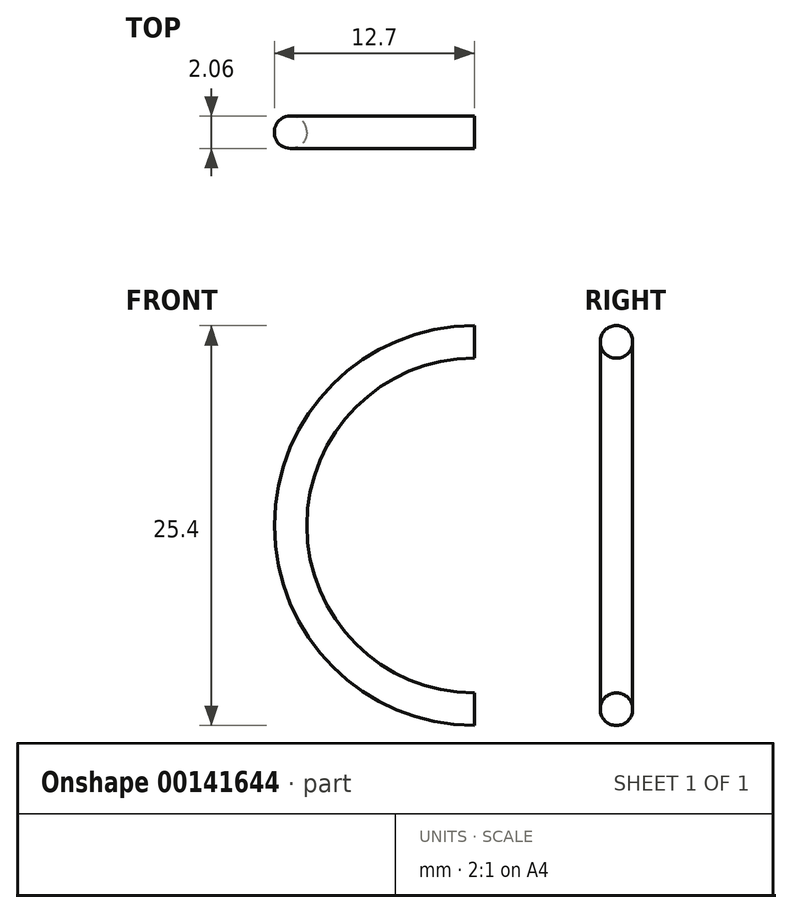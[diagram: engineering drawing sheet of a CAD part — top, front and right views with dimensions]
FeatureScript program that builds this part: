
annotation { "Feature Type Name" : "Feature", "Feature Type Description" : "" }
export const myFeature = defineFeature(function(context is Context, id is Id, definition is map)
    precondition{}
    {
        {
            var Q0;
            Q0=qCreatedBy(makeId("Front.planeOp"),FACE);
            var sketch = newSketch(context, id + "F0", { "sketchPlane" : qUnion([Q0])});
            skArc(sketch, "E0", {"start": v(0, 12.7) * mm, "mid": v(-12.7, 0) * mm, "end": v(0, -12.7) * mm});
            skArc(sketch, "E1", {"start": v(0, 10.63) * mm, "mid": v(-10.63, 0) * mm, "end": v(0, -10.63) * mm});
            skLineSegment(sketch, "E2", {"start": v(0, 12.7) * mm, "end": v(0, 10.63) * mm});
            skLineSegment(sketch, "E3", {"start": v(0, -10.63) * mm, "end": v(0, -12.7) * mm});
            skSolve(sketch);
        }
        {
            var Q0;
            Q0=makeQuery(id+"F0.imprint","IMPRINT",FACE,{"disambiguationData":[TD([[makeQuery(id+"F0.imprint","IMPRINT",EDGE,{"derivedFrom":sQuery(id+"F0.wireOp",EDGE,"E0")}),1.0]])]});
            extrude(context, id + "F1", {"entities" : qUnion([Q0]), "endBound" : BoundingType.SYMMETRIC, "depth" : 2.06 * mm});
        }
        {
            var Q0;
            Q0=makeQuery(id+"F1.opExtrude","CAP_EDGE",EDGE,{"disambiguationData":[OSD([sQuery(id+"F0.wireOp",EDGE,"E0")])],"isStart":false});
            var Q1;
            Q1=makeQuery(id+"F1.opExtrude","CAP_EDGE",EDGE,{"disambiguationData":[OSD([sQuery(id+"F0.wireOp",EDGE,"E1")])],"isStart":false});
            var Q2;
            Q2=makeQuery(id+"F1.opExtrude","CAP_EDGE",EDGE,{"disambiguationData":[OSD([sQuery(id+"F0.wireOp",EDGE,"E1")])],"isStart":true});
            var Q3;
            Q3=makeQuery(id+"F1.opExtrude","CAP_EDGE",EDGE,{"disambiguationData":[OSD([sQuery(id+"F0.wireOp",EDGE,"E0")])],"isStart":true});
            fillet(context, id + "F2", {"entities" : qUnion([Q0, Q1, Q2, Q3]), "radius" : 1.01 * mm, "tangentPropagation" : true, "allowEdgeOverflow" : false});
        }
    });
